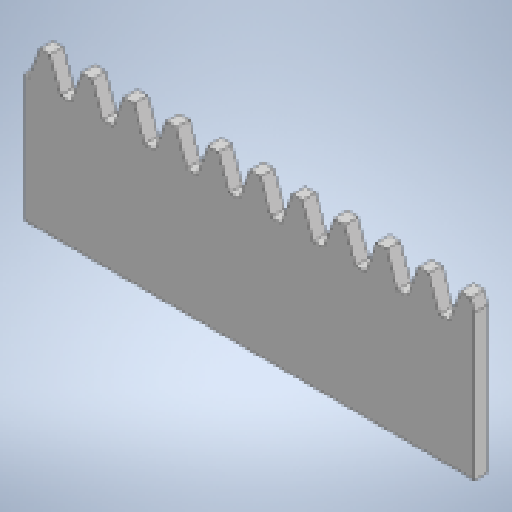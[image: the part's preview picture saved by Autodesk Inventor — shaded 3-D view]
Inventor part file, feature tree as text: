
AUTODESK INVENTOR PART (.ipt)
format: ipt  version: 2024 (Build 280153000, 153)  size: 217,088 bytes
history: native  units: mm
features: extrude x4, sketch x4, pattern_linear x1, projected_geometry x1
ambient origin geometry x8: Origin, YZ Plane, XZ Plane, XY Plane, X Axis, Y Axis, Z Axis, Center Point
bodies: Solid1 (feature_tree)
feature tree (10):
  extrude  "Extrusion1"  Depth=30.0mm TaperAngle=0.0deg
  extrude  "Extrusion2"  Depth=3.0mm
  pattern_linear  "Rectangular Pattern1"  Spacing1=0.0mm  [1 undecoded]
  extrude  "押し出し3"  Depth=10.0mm
  extrude  "押し出し4"  Depth=10.0mm
  sketch  "Sketch_4"  dims[d0=30.0mm d1=0.0mm d2=30.0mm d3=0.0mm]
  sketch  "Sketch_5"  dims[d4=120.0mm d6=9.42477mm d7=10.0mm d9=0.0mm d10=3.0mm d11=0.0mm d12=0.0mm d13=2.6mm d14=10.0mm d15=5.0mm d16=2.2mm d17=0.0mm d18=0.0mm]
  sketch  "スケッチ3"
  projected_geometry  "投影ループ1"
  sketch  "スケッチ4"
note: 1 required parameter value undecoded (feature->parameter linkage not recoverable at this tier; creation-order binding heuristic only, values carry confidence <= 0.55)
